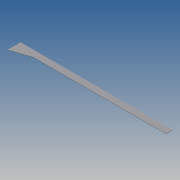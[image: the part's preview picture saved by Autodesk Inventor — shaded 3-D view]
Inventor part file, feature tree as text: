
AUTODESK INVENTOR PART (.ipt)
format: ipt  version: 2013 (Build 170138000, 138)  size: 69,632 bytes
history: native  units: in
note: dims shown in document units (in); Inventor stores cm internally (conversion verified against a paired STEP export)
features: extrude x1, sketch x1
ambient origin geometry x8: Origin, YZ Plane, XZ Plane, XY Plane, X Axis, Y Axis, Z Axis, Center Point
bodies: Solid1 (feature_tree)
feature tree (2):
  extrude  "Extrusion1"  Depth=20.0in
  sketch  "Sketch1"  dims[d0=60.0in d1=20.0in d2=40.0in d3=408.0in d4=408.0in d5=1.0in d6=0.0in]
